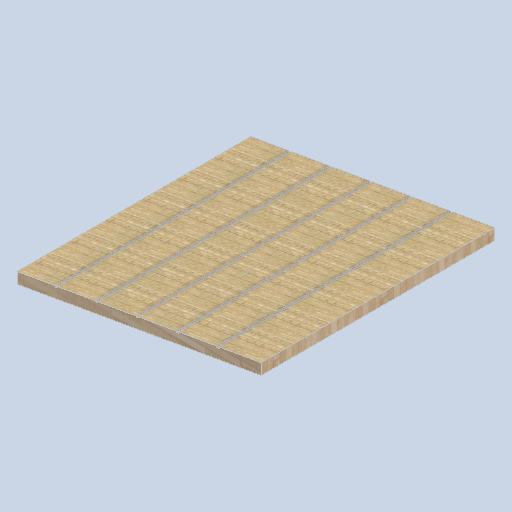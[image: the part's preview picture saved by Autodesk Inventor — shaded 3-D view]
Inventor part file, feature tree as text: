
AUTODESK INVENTOR PART (.ipt)
format: ipt  version: 2024.2 (Build 282272000, 272)  size: 253,440 bytes
history: native  units: in
note: dims shown in document units (in); Inventor stores cm internally (conversion verified against a paired STEP export)
features: sketch x4, other x3, plane x3
ambient origin geometry x8: Origin, YZ Plane, XZ Plane, XY Plane, X Axis, Y Axis, Z Axis, Center Point
bodies: Solid1 (feature_tree)
feature tree (10):
  other  "eave_panel_side_.ipt"
  other  "Solid1::eave_panel_side_.ipt"
  other  "TaggingFeature1"
  sketch  "Sketch1"  dims[d0=0.3937in]
  sketch  "Sketch2"
  sketch  "Sketch3"
  sketch  "Sketch4"
  plane  "Work Plane1"
  plane  "Work Plane2"
  plane  "Work Plane3"
